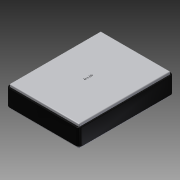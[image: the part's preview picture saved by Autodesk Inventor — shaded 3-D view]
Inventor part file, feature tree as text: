
AUTODESK INVENTOR PART (.ipt)
format: ipt  version: 2014 SP1 (Build 180222100, 222)  size: 463,360 bytes
history: native  units: mm
features: fillet x3, sketch x3, extrude x2, emboss x1
ambient origin geometry x8: Origin, YZ Plane, XZ Plane, XY Plane, X Axis, Y Axis, Z Axis, Center Point
bodies: Body1 (feature_tree)
feature tree (9):
  extrude  "Extrusion1"  Depth=111.76mm
  extrude  "Extrusion2"  Depth=2.54mm
  fillet  "Fillet1"  Radius=2.54mm
  fillet  "Fillet2"  Radius=33.02mm
  fillet  "Fillet3"  Radius=0.508mm
  emboss  "Emboss1"
  sketch  "Sketch1"  dims[d0=144.78mm d1=111.76mm]
  sketch  "Sketch2"  dims[d2=25.4mm d3=0.0mm d4=2.54mm d5=2.54mm d6=33.02mm d7=0.0mm d8=0.508mm]
  sketch  "Sketch3"  dims[d9=1.27mm d11=2.54mm d12=2.54mm d13=5.08mm d14=2.54mm d15=0.0mm]
